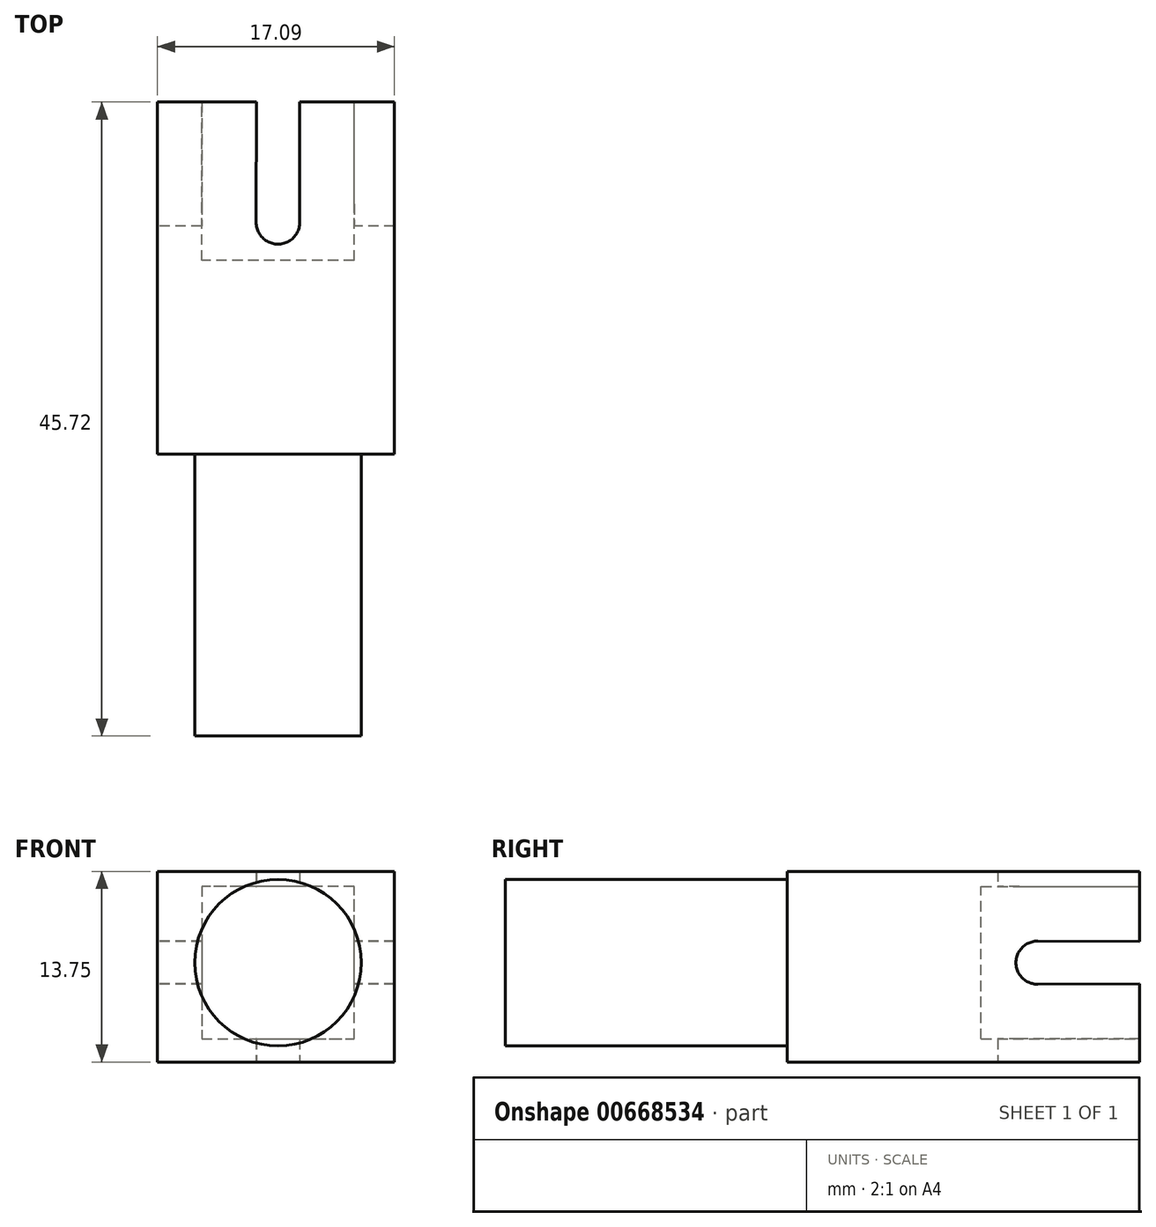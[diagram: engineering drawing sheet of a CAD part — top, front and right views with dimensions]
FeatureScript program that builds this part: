
annotation { "Feature Type Name" : "Feature", "Feature Type Description" : "" }
export const myFeature = defineFeature(function(context is Context, id is Id, definition is map)
    precondition{}
    {
        {
            var Q0;
            Q0=qCreatedBy(makeId("Front.planeOp"),FACE);
            var sketch = newSketch(context, id + "F0", { "sketchPlane" : qUnion([Q0])});
            skCircle(sketch, "E0", {"center": v(0, 0) * mm, "radius": 6 * mm});
            skSolve(sketch);
        }
        {
            var Q0;
            Q0=makeQuery(id+"F0.imprint","IMPRINT",FACE,{"disambiguationData":[TD([[makeQuery(id+"F0.imprint","IMPRINT",EDGE,{"derivedFrom":sQuery(id+"F0.wireOp",EDGE,"E0")}),1.0]])]});
            extrude(context, id + "F1", {"entities" : qUnion([Q0]), "depth" : 20.32 * mm, "offsetDistance" : 25.4 * mm});
        }
        {
            var Q0;
            Q0=makeQuery(id+"F1.opExtrude","CAP_FACE",FACE,{"disambiguationData":[OSD([sQuery(id+"F0.wireOp",EDGE,"E0")])],"isStart":true});
            var sketch = newSketch(context, id + "F2", { "sketchPlane" : qUnion([Q0])});
            skLineSegment(sketch, "E1.bottom", {"start": v(-8.4, 6.59) * mm, "end": v(8.69, 6.59) * mm});
            skLineSegment(sketch, "E1.top", {"start": v(-8.4, -7.16) * mm, "end": v(8.69, -7.16) * mm});
            skLineSegment(sketch, "E1.left", {"start": v(-8.4, 6.59) * mm, "end": v(-8.4, -7.16) * mm});
            skLineSegment(sketch, "E1.right", {"start": v(8.69, 6.59) * mm, "end": v(8.69, -7.16) * mm});
            skSolve(sketch);
        }
        {
            var Q0;
            Q0 = qSketchRegion(id + "F2", true);
            extrude(context, id + "F3", {"entities" : qUnion([Q0]), "operationType" : NewBodyOperationType.ADD, "depth" : 25.4 * mm, "offsetDistance" : 25.4 * mm});
        }
        {
            var Q0;
            Q0=makeQuery(id+"F3.opExtrude","CAP_FACE",FACE,{"disambiguationData":[OSD([sQuery(id+"F2.wireOp",EDGE,"E1.bottom"),sQuery(id+"F2.wireOp",EDGE,"E1.top"),sQuery(id+"F2.wireOp",EDGE,"E1.left"),sQuery(id+"F2.wireOp",EDGE,"E1.right")])],"isStart":false});
            var sketch = newSketch(context, id + "F4", { "sketchPlane" : qUnion([Q0])});
            skLineSegment(sketch, "E2", {"start": v(0, 5.5) * mm, "end": v(5.5, 5.5) * mm});
            skLineSegment(sketch, "E3", {"start": v(5.5, 5.5) * mm, "end": v(5.5, -5.5) * mm});
            skLineSegment(sketch, "E4", {"start": v(5.5, -5.5) * mm, "end": v(-5.5, -5.5) * mm});
            skLineSegment(sketch, "E5", {"start": v(-5.5, -5.5) * mm, "end": v(-5.5, 5.5) * mm});
            skLineSegment(sketch, "E6", {"start": v(-5.5, 5.5) * mm, "end": v(0, 5.5) * mm});
            skSolve(sketch);
        }
        {
            var Q0;
            Q0=makeQuery(id+"F4.imprint","IMPRINT",FACE,{"disambiguationData":[TD([[makeQuery(id+"F4.imprint","IMPRINT",EDGE,{"derivedFrom":sQuery(id+"F4.wireOp",EDGE,"A4xybUUC-eOZ0-e9Ol-FT8T-Y5batCkTaFNf")}),-1.0]])]});
            var Q1;
            Q1=makeQuery(id+"F4.imprint","IMPRINT",FACE,{"disambiguationData":[TD([[makeQuery(id+"F4.imprint","IMPRINT",EDGE,{"derivedFrom":sQuery(id+"F4.wireOp",EDGE,"E2")}),-1.0]])]});
            extrude(context, id + "F5", {"entities" : qUnion([Q0, Q1]), "operationType" : NewBodyOperationType.REMOVE, "oppositeDirection" : true, "depth" : 11.43 * mm, "offsetDistance" : 25.4 * mm});
        }
        {
            var Q0;
            Q0=makeQuery(id+"F3.opExtrude","SWEPT_FACE",FACE,{"disambiguationData":[OSD([sQuery(id+"F2.wireOp",EDGE,"E1.top")])]});
            var sketch = newSketch(context, id + "F6", { "sketchPlane" : qUnion([Q0])});
            skArc(sketch, "E7", {"start": v(1.57, -16.73) * mm, "mid": v(0, -15.16) * mm, "end": v(-1.57, -16.74) * mm});
            skLineSegment(sketch, "E8", {"start": v(-1.57, -16.73) * mm, "end": v(-1.56, -25.4) * mm});
            skLineSegment(sketch, "E9", {"start": v(1.57, -16.73) * mm, "end": v(1.57, -25.4) * mm});
            skLineSegment(sketch, "E10", {"start": v(-1.56, -25.4) * mm, "end": v(1.57, -25.4) * mm});
            skPoint(sketch, "E11.center.orphan", {"position": v(0, -22.25) * mm});
            skSolve(sketch);
        }
        {
            var Q0;
            {var subQ3=sQuery(id+"F6.wireOp",EDGE,"E7");Q0=makeQuery(id+"F6.imprint","IMPRINT",FACE,{"disambiguationData":[TD([[makeQuery(id+"F6.imprint","IMPRINT",EDGE,{"derivedFrom":subQ3}),1.0]])]});}
            extrude(context, id + "F7", {"entities" : qUnion([Q0]), "operationType" : NewBodyOperationType.REMOVE, "oppositeDirection" : true, "depth" : 25.4 * mm, "offsetDistance" : 25.4 * mm});
        }
        {
            var Q0;
            Q0=makeQuery(id+"F3.opExtrude","SWEPT_FACE",FACE,{"disambiguationData":[OSD([sQuery(id+"F2.wireOp",EDGE,"E1.right")])]});
            var sketch = newSketch(context, id + "F8", { "sketchPlane" : qUnion([Q0])});
            skArc(sketch, "E12", {"start": v(-18.04, -1.56) * mm, "mid": v(-16.47, 0) * mm, "end": v(-18.04, 1.56) * mm});
            skLineSegment(sketch, "E13", {"start": v(-18.03, 1.56) * mm, "end": v(-25.4, 1.53) * mm});
            skLineSegment(sketch, "E14", {"start": v(-18.03, -1.56) * mm, "end": v(-25.4, -1.53) * mm});
            skLineSegment(sketch, "E15", {"start": v(-25.4, -1.53) * mm, "end": v(-25.4, 1.53) * mm});
            skPoint(sketch, "E16.center.orphan", {"position": v(-23.2, 0) * mm});
            skLineSegment(sketch, "E17", {"start": v(-25.4, 1.53) * mm, "end": v(-25.4, -1.53) * mm});
            skSolve(sketch);
        }
        {
            var Q0;
            {var subQ1=sQuery(id+"F8.wireOp",EDGE,"E12");Q0=makeQuery(id+"F8.imprint","IMPRINT",FACE,{"disambiguationData":[TD([[makeQuery(id+"F8.imprint","IMPRINT",EDGE,{"derivedFrom":subQ1}),1.0]])]});}
            extrude(context, id + "F9", {"entities" : qUnion([Q0]), "operationType" : NewBodyOperationType.REMOVE, "oppositeDirection" : true, "depth" : 25.4 * mm, "offsetDistance" : 25.4 * mm});
        }
    });
